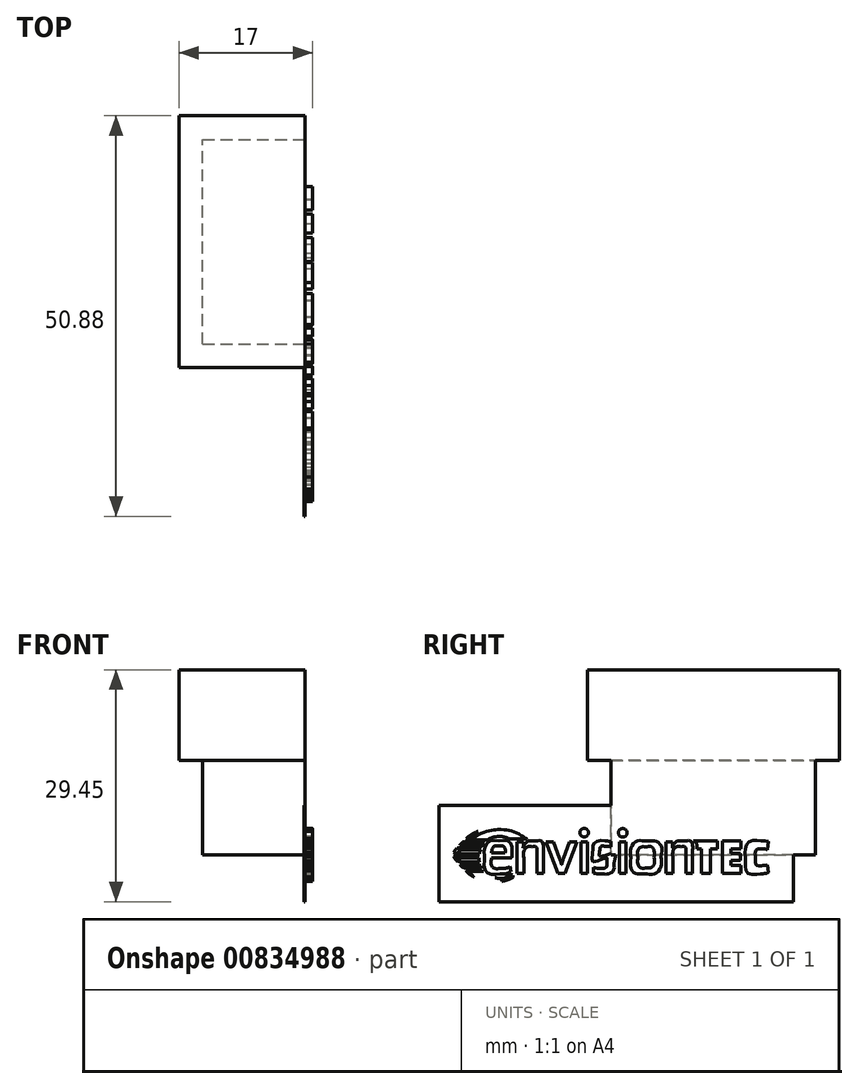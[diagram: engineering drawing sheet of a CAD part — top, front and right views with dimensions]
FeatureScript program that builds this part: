
annotation { "Feature Type Name" : "Feature", "Feature Type Description" : "" }
export const myFeature = defineFeature(function(context is Context, id is Id, definition is map)
    precondition{}
    {
        {
            var Q0;
            Q0=qCreatedBy(makeId("Top.planeOp"),FACE);
            var sketch = newSketch(context, id + "F0", { "sketchPlane" : qUnion([Q0])});
            skLineSegment(sketch, "E0.bottom", {"start": v(0, 0) * mm, "end": v(13, 0) * mm});
            skLineSegment(sketch, "E0.top", {"start": v(0, 26) * mm, "end": v(13, 26) * mm});
            skLineSegment(sketch, "E0.left", {"start": v(0, 0) * mm, "end": v(0, 26) * mm});
            skLineSegment(sketch, "E0.right", {"start": v(13, 0) * mm, "end": v(13, 26) * mm});
            skSolve(sketch);
        }
        {
            var Q0;
            Q0=makeQuery(id+"F0.imprint","IMPRINT",FACE,{"disambiguationData":[TD([[makeQuery(id+"F0.imprint","IMPRINT",EDGE,{"derivedFrom":sQuery(id+"F0.wireOp",EDGE,"E0.bottom")}),1.0]])]});
            extrude(context, id + "F1", {"entities" : qUnion([Q0]), "depth" : 22 * mm, "offsetDistance" : 25 * mm});
        }
        {
            var Q0;
            Q0=makeQuery(id+"F1.opExtrude","CAP_FACE",FACE,{"disambiguationData":[OSD([sQuery(id+"F0.wireOp",EDGE,"E0.bottom"),sQuery(id+"F0.wireOp",EDGE,"E0.top"),sQuery(id+"F0.wireOp",EDGE,"E0.left"),sQuery(id+"F0.wireOp",EDGE,"E0.right")])],"isStart":false});
            var sketch = newSketch(context, id + "F2", { "sketchPlane" : qUnion([Q0])});
            skLineSegment(sketch, "E1", {"start": v(13, 26) * mm, "end": v(13, 29) * mm});
            skLineSegment(sketch, "E2", {"start": v(13, 29) * mm, "end": v(-3, 29) * mm});
            skLineSegment(sketch, "E3", {"start": v(-3, 29) * mm, "end": v(-3, -3) * mm});
            skLineSegment(sketch, "E4", {"start": v(-3, -3) * mm, "end": v(13, -3) * mm});
            skLineSegment(sketch, "E5", {"start": v(13, -3) * mm, "end": v(13, 26) * mm});
            skSolve(sketch);
        }
        {
            var Q0;
            Q0=makeQuery(id+"F2.imprint","IMPRINT",FACE,{"disambiguationData":[TD([[makeQuery(id+"F2.imprint","IMPRINT",EDGE,{"derivedFrom":sQuery(id+"F2.wireOp",EDGE,"E1")}),1.0]])]});
            extrude(context, id + "F3", {"entities" : qUnion([Q0]), "oppositeDirection" : true, "depth" : 10 * mm, "offsetDistance" : 25 * mm});
        }
        {
            var Q0;
            Q0=makeQuery(id+"F3.opExtrude","CAP_FACE",FACE,{"disambiguationData":[OSD([sQuery(id+"F0.wireOp",EDGE,"E0.bottom"),sQuery(id+"F0.wireOp",EDGE,"E0.top"),sQuery(id+"F0.wireOp",EDGE,"E0.left"),sQuery(id+"F2.wireOp",EDGE,"E1"),sQuery(id+"F2.wireOp",EDGE,"E2"),sQuery(id+"F2.wireOp",EDGE,"E3"),sQuery(id+"F2.wireOp",EDGE,"E4"),sQuery(id+"F2.wireOp",EDGE,"E5")])],"isStart":true});
            var sketch = newSketch(context, id + "F4", { "sketchPlane" : qUnion([Q0])});
            skLineSegment(sketch, "E6.bottom", {"start": v(-3, 29) * mm, "end": v(13, 29) * mm});
            skLineSegment(sketch, "E6.top", {"start": v(-3, -3) * mm, "end": v(13, -3) * mm});
            skLineSegment(sketch, "E6.left", {"start": v(-3, 29) * mm, "end": v(-3, -3) * mm});
            skLineSegment(sketch, "E6.right", {"start": v(13, 29) * mm, "end": v(13, -3) * mm});
            skSolve(sketch);
        }
        {
            var Q0;
            Q0 = qSketchRegion(id + "F4", true);
            extrude(context, id + "F5", {"entities" : qUnion([Q0]), "operationType" : NewBodyOperationType.ADD, "depth" : 1.5 * mm, "offsetDistance" : 25 * mm});
        }
        {
            var Q0;
            Q0=makeQuery(id+"F1.opExtrude","SWEPT_FACE",FACE,{"disambiguationData":[OSD([sQuery(id+"F0.wireOp",EDGE,"E0.right")])]});
            var sketch = newSketch(context, id + "F6", { "sketchPlane" : qUnion([Q0])});
            skFitSpline(sketch, "E7", {"points": [v(-18.49, 1.44) * mm, v(-18.63, 1.49) * mm, v(-18.77, 1.54) * mm, v(-18.91, 1.58) * mm]});
            skFitSpline(sketch, "E8", {"points": [v(-18.91, 1.58) * mm, v(-19.01, 1.48) * mm, v(-19.1, 1.38) * mm, v(-19.19, 1.28) * mm]});
            skFitSpline(sketch, "E9", {"points": [v(-19.19, 1.28) * mm, v(-19.05, 1.23) * mm, v(-18.9, 1.18) * mm, v(-18.76, 1.14) * mm]});
            skFitSpline(sketch, "E10", {"points": [v(-18.76, 1.14) * mm, v(-18.63, 1.29) * mm, v(-18.6, 1.31) * mm, v(-18.49, 1.44) * mm]});
            skFitSpline(sketch, "E11", {"points": [v(-16.8, -0.4) * mm, v(-17.67, -0.4) * mm, v(-18.55, -0.4) * mm, v(-19.43, -0.4) * mm]});
            skFitSpline(sketch, "E12", {"points": [v(-19.43, -0.4) * mm, v(-19.36, -0.5) * mm, v(-19.1, -0.85) * mm, v(-19.06, -0.92) * mm]});
            skFitSpline(sketch, "E13", {"points": [v(-19.06, -0.92) * mm, v(-18.28, -0.92) * mm, v(-17.5, -0.92) * mm, v(-16.7, -0.92) * mm]});
            skFitSpline(sketch, "E14", {"points": [v(-16.7, -0.92) * mm, v(-16.76, -0.73) * mm, v(-16.79, -0.56) * mm, v(-16.8, -0.4) * mm]});
            skFitSpline(sketch, "E15", {"points": [v(-18.76, -1.4) * mm, v(-18.9, -1.35) * mm, v(-19.04, -1.3) * mm, v(-19.19, -1.25) * mm]});
            skFitSpline(sketch, "E16", {"points": [v(-19.19, -1.25) * mm, v(-19.1, -1.35) * mm, v(-19, -1.46) * mm, v(-18.91, -1.56) * mm]});
            skFitSpline(sketch, "E17", {"points": [v(-18.91, -1.56) * mm, v(-18.77, -1.6) * mm, v(-18.63, -1.65) * mm, v(-18.49, -1.7) * mm]});
            skFitSpline(sketch, "E18", {"points": [v(-18.49, -1.7) * mm, v(-18.58, -1.6) * mm, v(-18.67, -1.49) * mm, v(-18.76, -1.4) * mm]});
            skFitSpline(sketch, "E19", {"points": [v(-12.46, -2.63) * mm, v(-14.33, -3.43) * mm, v(-15.5, -2.93) * mm, v(-16.15, -2.17) * mm]});
            skFitSpline(sketch, "E20", {"points": [v(-16.15, -2.17) * mm, v(-16.72, -2.17) * mm, v(-17.28, -2.17) * mm, v(-17.84, -2.17) * mm]});
            skFitSpline(sketch, "E21", {"points": [v(-17.84, -2.17) * mm, v(-17.12, -2.75) * mm, v(-17.02, -2.77) * mm, v(-16.6, -2.98) * mm]});
            skFitSpline(sketch, "E22", {"points": [v(-15.52, -3.3) * mm, v(-15.33, -3.34) * mm, v(-15.12, -3.35) * mm, v(-14.91, -3.37) * mm]});
            skFitSpline(sketch, "E23", {"points": [v(-16.6, -2.98) * mm, v(-16.28, -3.13) * mm, v(-15.9, -3.22) * mm, v(-15.52, -3.3) * mm]});
            skFitSpline(sketch, "E24", {"points": [v(-14.46, -3.37) * mm, v(-13.84, -3.35) * mm, v(-13.16, -3.2) * mm, v(-12.43, -2.88) * mm]});
            skFitSpline(sketch, "E25", {"points": [v(-14.91, -3.37) * mm, v(-14.77, -3.37) * mm, v(-14.62, -3.38) * mm, v(-14.46, -3.37) * mm]});
            skFitSpline(sketch, "E26", {"points": [v(-12.43, -2.88) * mm, v(-12.44, -2.8) * mm, v(-12.45, -2.71) * mm, v(-12.46, -2.63) * mm]});
            skFitSpline(sketch, "E27", {"points": [v(-16.33, 1.13) * mm, v(-16.26, 1.23) * mm, v(-16.18, 1.33) * mm, v(-16.1, 1.42) * mm]});
            skFitSpline(sketch, "E28", {"points": [v(-16.1, 1.42) * mm, v(-16.86, 1.42) * mm, v(-17.63, 1.42) * mm, v(-18.39, 1.42) * mm]});
            skFitSpline(sketch, "E29", {"points": [v(-18.39, 1.42) * mm, v(-18.48, 1.32) * mm, v(-18.57, 1.23) * mm, v(-18.66, 1.13) * mm]});
            skFitSpline(sketch, "E30", {"points": [v(-18.66, 1.13) * mm, v(-17.88, 1.13) * mm, v(-17.1, 1.13) * mm, v(-16.33, 1.13) * mm]});
            skFitSpline(sketch, "E31", {"points": [v(-19.43, 0.14) * mm, v(-18.53, 0.14) * mm, v(-17.62, 0.13) * mm, v(-16.72, 0.13) * mm]});
            skFitSpline(sketch, "E32", {"points": [v(-16.72, 0.13) * mm, v(-16.68, 0.32) * mm, v(-16.61, 0.49) * mm, v(-16.54, 0.65) * mm]});
            skFitSpline(sketch, "E33", {"points": [v(-16.54, 0.65) * mm, v(-17.38, 0.65) * mm, v(-18.23, 0.65) * mm, v(-19.07, 0.65) * mm]});
            skFitSpline(sketch, "E34", {"points": [v(-19.07, 0.65) * mm, v(-19.2, 0.48) * mm, v(-19.3, 0.3) * mm, v(-19.43, 0.14) * mm]});
            skFitSpline(sketch, "E35", {"points": [v(-17, 0.88) * mm, v(-18.27, 0.88) * mm, v(-19.52, 0.88) * mm]});
            skFitSpline(sketch, "E36", {"points": [v(-19.52, 0.88) * mm, v(-19.28, 0.8) * mm, v(-19.03, 0.71) * mm]});
            skFitSpline(sketch, "E37", {"points": [v(-19.03, 0.71) * mm, v(-17.77, 0.71) * mm, v(-16.51, 0.71) * mm]});
            skFitSpline(sketch, "E38", {"points": [v(-16.51, 0.71) * mm, v(-16.76, 0.8) * mm, v(-17, 0.88) * mm]});
            skFitSpline(sketch, "E39", {"points": [v(-16.08, 1.5) * mm, v(-16.32, 1.57) * mm, v(-16.56, 1.65) * mm]});
            skFitSpline(sketch, "E40", {"points": [v(-16.56, 1.65) * mm, v(-17.7, 1.65) * mm, v(-18.84, 1.65) * mm]});
            skFitSpline(sketch, "E41", {"points": [v(-18.84, 1.65) * mm, v(-18.6, 1.57) * mm, v(-18.36, 1.5) * mm]});
            skFitSpline(sketch, "E42", {"points": [v(-18.36, 1.5) * mm, v(-17.22, 1.5) * mm, v(-16.08, 1.5) * mm]});
            skFitSpline(sketch, "E43", {"points": [v(-18.41, 2.07) * mm, v(-18.27, 2.03) * mm, v(-18.12, 1.98) * mm, v(-17.97, 1.93) * mm]});
            skFitSpline(sketch, "E44", {"points": [v(-17.97, 1.93) * mm, v(-16.13, 3.5) * mm, v(-12.93, 3.96) * mm, v(-10.72, 2) * mm]});
            skFitSpline(sketch, "E45", {"points": [v(-10.72, 2) * mm, v(-10.7, 2) * mm, v(-10.7, 2) * mm, v(-10.69, 2) * mm]});
            skFitSpline(sketch, "E46", {"points": [v(10.47, 1.74) * mm, v(10.78, 1.6) * mm, v(10.94, 1.14) * mm, v(10.95, 0.77) * mm]});
            skFitSpline(sketch, "E47", {"points": [v(10.95, 0.77) * mm, v(11.14, 0.77) * mm, v(11.32, 0.77) * mm, v(11.5, 0.77) * mm]});
            skFitSpline(sketch, "E48", {"points": [v(11.5, 0.77) * mm, v(11.5, -0.26) * mm, v(11.5, -1.3) * mm, v(11.5, -2.34) * mm]});
            skFitSpline(sketch, "E49", {"points": [v(11.5, -2.34) * mm, v(11.89, -2.34) * mm, v(12.26, -2.34) * mm, v(12.64, -2.34) * mm]});
            skFitSpline(sketch, "E50", {"points": [v(12.64, -2.34) * mm, v(12.64, -1.3) * mm, v(12.64, -0.26) * mm, v(12.64, 0.77) * mm]});
            skFitSpline(sketch, "E51", {"points": [v(12.64, 0.77) * mm, v(12.93, 0.77) * mm, v(13.23, 0.77) * mm, v(13.52, 0.77) * mm]});
            skFitSpline(sketch, "E52", {"points": [v(13.52, 0.77) * mm, v(13.52, 1.1) * mm, v(13.52, 1.42) * mm, v(13.52, 1.74) * mm]});
            skFitSpline(sketch, "E53", {"points": [v(13.52, 1.74) * mm, v(12.5, 1.74) * mm, v(11.49, 1.74) * mm, v(10.47, 1.74) * mm]});
            skFitSpline(sketch, "E54", {"points": [v(10.37, -2.33) * mm, v(10.37, -1.4) * mm, v(10.37, -0.46) * mm, v(10.37, 0.47) * mm]});
            skFitSpline(sketch, "E55", {"points": [v(10.37, 0.47) * mm, v(10.37, 1.18) * mm, v(10.09, 1.76) * mm, v(9.18, 1.76) * mm, v(8.5, 1.76) * mm, v(8.02, 1.4) * mm, v(7.78, 0.88) * mm]});
            skFitSpline(sketch, "E56", {"points": [v(7.78, 0.88) * mm, v(7.78, 0.89) * mm, v(7.78, 0.9) * mm, v(7.77, 0.9) * mm]});
            skFitSpline(sketch, "E57", {"points": [v(7.78, 0.88) * mm, v(7.78, 0.89) * mm, v(7.78, 0.9) * mm, v(7.77, 0.9) * mm]});
            skFitSpline(sketch, "E58", {"points": [v(7.77, 0.9) * mm, v(7.81, 1.12) * mm, v(7.83, 1.46) * mm, v(7.83, 1.67) * mm]});
            skFitSpline(sketch, "E59", {"points": [v(7.83, 1.67) * mm, v(7.56, 1.67) * mm, v(7.28, 1.67) * mm, v(7, 1.67) * mm]});
            skFitSpline(sketch, "E60", {"points": [v(7, 1.67) * mm, v(7, 0.34) * mm, v(7, -1) * mm, v(7, -2.33) * mm]});
            skFitSpline(sketch, "E61", {"points": [v(7, -2.33) * mm, v(7.3, -2.33) * mm, v(7.58, -2.33) * mm, v(7.87, -2.33) * mm]});
            skFitSpline(sketch, "E62", {"points": [v(7.87, -2.33) * mm, v(7.87, -1.68) * mm, v(7.87, -1.04) * mm, v(7.87, -0.4) * mm]});
            skFitSpline(sketch, "E63", {"points": [v(7.87, -0.4) * mm, v(7.87, 0.4) * mm, v(8.31, 1.04) * mm, v(8.92, 1.04) * mm, v(9.38, 1.04) * mm, v(9.51, 0.75) * mm, v(9.51, 0.25) * mm]});
            skFitSpline(sketch, "E64", {"points": [v(9.51, 0.25) * mm, v(9.51, -0.61) * mm, v(9.51, -1.47) * mm, v(9.51, -2.33) * mm]});
            skFitSpline(sketch, "E65", {"points": [v(9.51, -2.33) * mm, v(9.8, -2.33) * mm, v(10.08, -2.33) * mm, v(10.37, -2.33) * mm]});
            skFitSpline(sketch, "E66", {"points": [v(2.54, -0.38) * mm, v(2.54, -1.79) * mm, v(3.26, -2.4) * mm, v(4.37, -2.4) * mm, v(5.56, -2.4) * mm, v(6.36, -1.48) * mm, v(6.36, -0.25) * mm]});
            skFitSpline(sketch, "E67", {"points": [v(6.36, -0.25) * mm, v(6.36, 1.16) * mm, v(5.6, 1.76) * mm, v(4.53, 1.76) * mm, v(3.32, 1.76) * mm, v(2.54, 0.83) * mm, v(2.54, -0.38) * mm]});
            skFitSpline(sketch, "E68", {"points": [v(3.43, -0.3) * mm, v(3.43, 0.63) * mm, v(3.94, 1.03) * mm, v(4.46, 1.03) * mm, v(5.14, 1.03) * mm, v(5.48, 0.55) * mm, v(5.48, -0.3) * mm]});
            skFitSpline(sketch, "E69", {"points": [v(5.48, -0.3) * mm, v(5.48, -1.23) * mm, v(5, -1.67) * mm, v(4.45, -1.67) * mm, v(3.78, -1.67) * mm, v(3.43, -1.2) * mm, v(3.43, -0.3) * mm]});
            skFitSpline(sketch, "E70", {"points": [v(1.93, 1.67) * mm, v(1.5, 1.67) * mm, v(1.07, 1.67) * mm]});
            skFitSpline(sketch, "E71", {"points": [v(1.07, 1.67) * mm, v(1.07, -0.33) * mm, v(1.07, -2.33) * mm]});
            skFitSpline(sketch, "E72", {"points": [v(1.07, -2.33) * mm, v(1.5, -2.33) * mm, v(1.93, -2.33) * mm]});
            skFitSpline(sketch, "E73", {"points": [v(1.93, -2.33) * mm, v(1.93, -0.33) * mm, v(1.93, 1.67) * mm]});
            skFitSpline(sketch, "E74", {"points": [v(0.36, -1.11) * mm, v(0.36, 0.22) * mm, v(-1.4, -0.18) * mm, v(-1.4, 0.6) * mm, v(-1.4, 0.9) * mm, v(-1.18, 1.1) * mm, v(-0.7, 1.1) * mm, v(-0.44, 1.1) * mm, v(-0.16, 1.05) * mm, v(0.08, 0.98) * mm]});
            skFitSpline(sketch, "E75", {"points": [v(0.08, 0.98) * mm, v(0.09, 1.22) * mm, v(0.1, 1.45) * mm, v(0.1, 1.68) * mm]});
            skFitSpline(sketch, "E76", {"points": [v(0.1, 1.68) * mm, v(-0.14, 1.72) * mm, v(-0.41, 1.76) * mm, v(-0.64, 1.76) * mm, v(-1.73, 1.76) * mm, v(-2.3, 1.2) * mm, v(-2.3, 0.51) * mm, v(-2.3, -0.87) * mm, v(-0.54, -0.39) * mm, v(-0.54, -1.2) * mm, v(-0.54, -1.52) * mm, v(-0.86, -1.72) * mm, v(-1.33, -1.72) * mm, v(-1.63, -1.72) * mm, v(-1.95, -1.67) * mm, v(-2.2, -1.6) * mm]});
            skFitSpline(sketch, "E77", {"points": [v(-2.2, -1.6) * mm, v(-2.2, -1.84) * mm, v(-2.21, -2.08) * mm, v(-2.22, -2.33) * mm]});
            skFitSpline(sketch, "E78", {"points": [v(-2.22, -2.33) * mm, v(-1.97, -2.38) * mm, v(-1.67, -2.4) * mm, v(-1.38, -2.4) * mm, v(-0.3, -2.4) * mm, v(0.36, -1.86) * mm, v(0.36, -1.11) * mm]});
            skFitSpline(sketch, "E79", {"points": [v(-2.98, 1.67) * mm, v(-3.41, 1.67) * mm, v(-3.84, 1.67) * mm]});
            skFitSpline(sketch, "E80", {"points": [v(-3.84, 1.67) * mm, v(-3.84, -0.33) * mm, v(-3.84, -2.33) * mm]});
            skFitSpline(sketch, "E81", {"points": [v(-3.84, -2.33) * mm, v(-3.41, -2.33) * mm, v(-2.98, -2.33) * mm]});
            skFitSpline(sketch, "E82", {"points": [v(-2.98, -2.33) * mm, v(-2.98, -0.33) * mm, v(-2.98, 1.67) * mm]});
            skFitSpline(sketch, "E83", {"points": [v(-4.35, 1.67) * mm, v(-4.65, 1.67) * mm, v(-4.96, 1.67) * mm, v(-5.27, 1.67) * mm]});
            skFitSpline(sketch, "E84", {"points": [v(-5.27, 1.67) * mm, v(-5.53, 0.96) * mm, v(-5.78, 0.24) * mm, v(-6.04, -0.48) * mm]});
            skFitSpline(sketch, "E85", {"points": [v(-6.04, -0.48) * mm, v(-6.13, -0.73) * mm, v(-6.2, -1.02) * mm, v(-6.27, -1.27) * mm]});
            skFitSpline(sketch, "E86", {"points": [v(-6.27, -1.27) * mm, v(-6.27, -1.27) * mm, v(-6.28, -1.27) * mm, v(-6.28, -1.27) * mm]});
            skFitSpline(sketch, "E87", {"points": [v(-6.27, -1.27) * mm, v(-6.27, -1.27) * mm, v(-6.28, -1.27) * mm, v(-6.28, -1.27) * mm]});
            skFitSpline(sketch, "E88", {"points": [v(-6.28, -1.27) * mm, v(-6.35, -1) * mm, v(-6.44, -0.72) * mm, v(-6.54, -0.44) * mm]});
            skFitSpline(sketch, "E89", {"points": [v(-6.54, -0.44) * mm, v(-6.79, 0.26) * mm, v(-7.04, 0.97) * mm, v(-7.29, 1.67) * mm]});
            skFitSpline(sketch, "E90", {"points": [v(-7.29, 1.67) * mm, v(-7.6, 1.67) * mm, v(-7.92, 1.67) * mm, v(-8.24, 1.67) * mm]});
            skFitSpline(sketch, "E91", {"points": [v(-8.24, 1.67) * mm, v(-7.74, 0.34) * mm, v(-7.24, -1) * mm, v(-6.74, -2.33) * mm]});
            skFitSpline(sketch, "E92", {"points": [v(-6.74, -2.33) * mm, v(-6.44, -2.33) * mm, v(-6.15, -2.33) * mm, v(-5.86, -2.33) * mm]});
            skFitSpline(sketch, "E93", {"points": [v(-5.86, -2.33) * mm, v(-5.35, -1) * mm, v(-4.85, 0.34) * mm, v(-4.35, 1.67) * mm]});
            skFitSpline(sketch, "E94", {"points": [v(-8.57, -2.33) * mm, v(-8.57, -1.4) * mm, v(-8.57, -0.46) * mm, v(-8.57, 0.47) * mm]});
            skFitSpline(sketch, "E95", {"points": [v(-8.57, 0.47) * mm, v(-8.57, 1.18) * mm, v(-8.85, 1.76) * mm, v(-9.76, 1.76) * mm, v(-10.44, 1.76) * mm, v(-10.92, 1.4) * mm, v(-11.16, 0.88) * mm]});
            skFitSpline(sketch, "E96", {"points": [v(-11.16, 0.88) * mm, v(-11.16, 0.89) * mm, v(-11.16, 0.9) * mm, v(-11.16, 0.9) * mm]});
            skFitSpline(sketch, "E97", {"points": [v(-11.16, 0.88) * mm, v(-11.16, 0.89) * mm, v(-11.16, 0.9) * mm, v(-11.16, 0.9) * mm]});
            skFitSpline(sketch, "E98", {"points": [v(-11.16, 0.9) * mm, v(-11.12, 1.12) * mm, v(-11.1, 1.46) * mm, v(-11.1, 1.67) * mm]});
            skFitSpline(sketch, "E99", {"points": [v(-11.1, 1.67) * mm, v(-11.38, 1.67) * mm, v(-11.65, 1.67) * mm, v(-11.93, 1.67) * mm]});
            skFitSpline(sketch, "E100", {"points": [v(-11.93, 1.67) * mm, v(-11.93, 0.34) * mm, v(-11.93, -1) * mm, v(-11.93, -2.33) * mm]});
            skFitSpline(sketch, "E101", {"points": [v(-11.93, -2.33) * mm, v(-11.64, -2.33) * mm, v(-11.35, -2.33) * mm, v(-11.07, -2.33) * mm]});
            skFitSpline(sketch, "E102", {"points": [v(-11.07, -2.33) * mm, v(-11.07, -1.68) * mm, v(-11.07, -1.04) * mm, v(-11.07, -0.4) * mm]});
            skFitSpline(sketch, "E103", {"points": [v(-11.07, -0.4) * mm, v(-11.07, 0.4) * mm, v(-10.62, 1.04) * mm, v(-10.02, 1.04) * mm, v(-9.56, 1.04) * mm, v(-9.42, 0.75) * mm, v(-9.42, 0.25) * mm]});
            skFitSpline(sketch, "E104", {"points": [v(-9.42, 0.25) * mm, v(-9.42, -0.61) * mm, v(-9.42, -1.47) * mm, v(-9.42, -2.33) * mm]});
            skFitSpline(sketch, "E105", {"points": [v(-9.42, -2.33) * mm, v(-9.14, -2.33) * mm, v(-8.85, -2.33) * mm, v(-8.57, -2.33) * mm]});
            skFitSpline(sketch, "E106", {"points": [v(20, -2.26) * mm, v(19.96, -1.92) * mm, v(19.91, -1.59) * mm, v(19.87, -1.25) * mm]});
            skFitSpline(sketch, "E107", {"points": [v(19.87, -1.25) * mm, v(19.7, -1.33) * mm, v(19.42, -1.37) * mm, v(19.25, -1.37) * mm, v(18.61, -1.37) * mm, v(18.34, -0.99) * mm, v(18.34, -0.28) * mm, v(18.34, 0.38) * mm, v(18.67, 0.75) * mm, v(19.2, 0.75) * mm, v(19.44, 0.75) * mm, v(19.67, 0.71) * mm, v(19.87, 0.66) * mm]});
            skFitSpline(sketch, "E108", {"points": [v(19.87, 0.66) * mm, v(19.9, 1) * mm, v(19.95, 1.34) * mm, v(20, 1.68) * mm]});
            skFitSpline(sketch, "E109", {"points": [v(20, 1.68) * mm, v(19.76, 1.74) * mm, v(19.47, 1.77) * mm, v(19.2, 1.77) * mm, v(17.87, 1.77) * mm, v(17.1, 0.9) * mm, v(17.1, -0.47) * mm, v(17.1, -1.3) * mm, v(17.43, -2.4) * mm, v(19.04, -2.4) * mm, v(19.36, -2.4) * mm, v(19.72, -2.35) * mm, v(20, -2.26) * mm]});
            skFitSpline(sketch, "E110", {"points": [v(16.52, -2.34) * mm, v(16.52, -1.86) * mm, v(16.52, -1.37) * mm]});
            skFitSpline(sketch, "E111", {"points": [v(16.52, -1.37) * mm, v(15.9, -1.37) * mm, v(15.26, -1.37) * mm]});
            skFitSpline(sketch, "E112", {"points": [v(15.26, -1.37) * mm, v(15.26, -1.04) * mm, v(15.26, -0.7) * mm]});
            skFitSpline(sketch, "E113", {"points": [v(15.26, -0.7) * mm, v(15.86, -0.7) * mm, v(16.46, -0.7) * mm]});
            skFitSpline(sketch, "E114", {"points": [v(16.46, -0.7) * mm, v(16.46, -0.25) * mm, v(16.46, 0.21) * mm]});
            skFitSpline(sketch, "E115", {"points": [v(16.46, 0.21) * mm, v(15.86, 0.21) * mm, v(15.26, 0.21) * mm]});
            skFitSpline(sketch, "E116", {"points": [v(15.26, 0.21) * mm, v(15.26, 0.5) * mm, v(15.26, 0.79) * mm]});
            skFitSpline(sketch, "E117", {"points": [v(15.26, 0.79) * mm, v(15.9, 0.79) * mm, v(16.52, 0.79) * mm]});
            skFitSpline(sketch, "E118", {"points": [v(16.52, 0.79) * mm, v(16.52, 1.27) * mm, v(16.52, 1.74) * mm]});
            skFitSpline(sketch, "E119", {"points": [v(16.52, 1.74) * mm, v(15.33, 1.74) * mm, v(14.13, 1.74) * mm]});
            skFitSpline(sketch, "E120", {"points": [v(14.13, 1.74) * mm, v(14.13, -0.3) * mm, v(14.13, -2.34) * mm]});
            skFitSpline(sketch, "E121", {"points": [v(14.13, -2.34) * mm, v(15.33, -2.34) * mm, v(16.52, -2.34) * mm]});
            skFitSpline(sketch, "E122", {"points": [v(-12.59, 0.02) * mm, v(-12.59, 0.98) * mm, v(-13.08, 1.76) * mm, v(-14.23, 1.76) * mm, v(-15.4, 1.76) * mm, v(-16.06, 0.86) * mm, v(-16.06, -0.36) * mm, v(-16.06, -1.77) * mm, v(-15.38, -2.42) * mm, v(-14.12, -2.42) * mm, v(-13.63, -2.42) * mm, v(-13.14, -2.33) * mm, v(-12.73, -2.16) * mm]});
            skFitSpline(sketch, "E123", {"points": [v(-12.73, -2.16) * mm, v(-12.76, -1.93) * mm, v(-12.79, -1.7) * mm, v(-12.81, -1.47) * mm]});
            skFitSpline(sketch, "E124", {"points": [v(-12.81, -1.47) * mm, v(-13.14, -1.63) * mm, v(-13.57, -1.73) * mm, v(-13.99, -1.73) * mm, v(-14.79, -1.73) * mm, v(-15.2, -1.31) * mm, v(-15.17, -0.38) * mm]});
            skFitSpline(sketch, "E125", {"points": [v(-12.81, -1.47) * mm, v(-13.14, -1.63) * mm, v(-13.57, -1.73) * mm, v(-13.99, -1.73) * mm, v(-14.79, -1.73) * mm, v(-15.2, -1.31) * mm, v(-15.17, -0.38) * mm]});
            skFitSpline(sketch, "E126", {"points": [v(-15.17, -0.38) * mm, v(-14.32, -0.38) * mm, v(-13.46, -0.38) * mm, v(-12.6, -0.38) * mm]});
            skFitSpline(sketch, "E127", {"points": [v(-12.6, -0.38) * mm, v(-12.6, -0.23) * mm, v(-12.59, -0.09) * mm, v(-12.59, 0.02) * mm]});
            skFitSpline(sketch, "E128", {"points": [v(-13.45, 0.23) * mm, v(-14.02, 0.23) * mm, v(-14.59, 0.23) * mm, v(-15.16, 0.23) * mm]});
            skFitSpline(sketch, "E129", {"points": [v(-15.16, 0.23) * mm, v(-15.09, 0.77) * mm, v(-14.75, 1.12) * mm, v(-14.26, 1.12) * mm, v(-13.75, 1.12) * mm, v(-13.43, 0.78) * mm, v(-13.45, 0.23) * mm]});
            skFitSpline(sketch, "E130", {"points": [v(-18.4, -1.95) * mm, v(-18.16, -2.03) * mm, v(-17.91, -2.1) * mm]});
            skFitSpline(sketch, "E131", {"points": [v(-17.91, -2.1) * mm, v(-17.05, -2.1) * mm, v(-16.2, -2.1) * mm]});
            skFitSpline(sketch, "E132", {"points": [v(-16.2, -2.1) * mm, v(-16.44, -2.03) * mm, v(-16.68, -1.95) * mm]});
            skFitSpline(sketch, "E133", {"points": [v(-16.68, -1.95) * mm, v(-17.54, -1.95) * mm, v(-18.4, -1.95) * mm]});
            skFitSpline(sketch, "E134", {"points": [v(-17.85, 1.9) * mm, v(-17.16, 1.9) * mm, v(-16.48, 1.9) * mm, v(-15.8, 1.9) * mm, v(-15.76, 1.9) * mm, v(-15.72, 1.9) * mm, v(-15.68, 1.9) * mm]});
            skFitSpline(sketch, "E135", {"points": [v(-14.87, 2.27) * mm, v(-14.02, 2.44) * mm, v(-13.15, 2.24) * mm, v(-12.84, 2) * mm]});
            skFitSpline(sketch, "E136", {"points": [v(-12.84, 2) * mm, v(-11.25, 2) * mm, v(-11.25, 2) * mm]});
            skFitSpline(sketch, "E137", {"points": [v(-11.25, 2) * mm, v(-11.25, 2) * mm, v(-10.8, 2) * mm]});
            skFitSpline(sketch, "E138", {"points": [v(-14.33, 3.21) * mm, v(-14.33, 3.21) * mm, v(-14.33, 3.21) * mm, v(-14.33, 3.21) * mm]});
            skFitSpline(sketch, "E139", {"points": [v(-14.33, 3.21) * mm, v(-14.33, 3.21) * mm, v(-14.33, 3.21) * mm, v(-14.33, 3.21) * mm]});
            skFitSpline(sketch, "E140", {"points": [v(-20, -0.18) * mm, v(-19.73, -0.25) * mm, v(-19.46, -0.33) * mm]});
            skFitSpline(sketch, "E141", {"points": [v(-19.46, -0.33) * mm, v(-18.13, -0.33) * mm, v(-16.8, -0.33) * mm]});
            skFitSpline(sketch, "E142", {"points": [v(-16.8, -0.33) * mm, v(-17.03, -0.25) * mm, v(-17.26, -0.18) * mm]});
            skFitSpline(sketch, "E143", {"points": [v(-17.26, -0.18) * mm, v(-18.63, -0.18) * mm, v(-20, -0.18) * mm]});
            skFitSpline(sketch, "E144", {"points": [v(-14.7, -2.92) * mm, v(-14.26, -3) * mm, v(-13.4, -3) * mm, v(-12.49, -2.54) * mm]});
            skFitSpline(sketch, "E145", {"points": [v(-12.49, -2.54) * mm, v(-12.57, -2.52) * mm, v(-12.65, -2.5) * mm, v(-12.73, -2.47) * mm]});
            skFitSpline(sketch, "E146", {"points": [v(-12.73, -2.47) * mm, v(-13.67, -2.98) * mm, v(-14.7, -2.92) * mm]});
            skFitSpline(sketch, "E147", {"points": [v(-20, -0.24) * mm, v(-19.86, -0.37) * mm, v(-19.73, -0.6) * mm, v(-19.6, -0.77) * mm]});
            skFitSpline(sketch, "E148", {"points": [v(-19.6, -0.77) * mm, v(-19.45, -0.82) * mm, v(-19.3, -0.86) * mm, v(-19.16, -0.91) * mm]});
            skFitSpline(sketch, "E149", {"points": [v(-19.16, -0.91) * mm, v(-19.31, -0.7) * mm, v(-19.5, -0.42) * mm, v(-19.53, -0.4) * mm]});
            skFitSpline(sketch, "E150", {"points": [v(-19.53, -0.4) * mm, v(-19.69, -0.34) * mm, v(-19.84, -0.29) * mm, v(-20, -0.24) * mm]});
            skFitSpline(sketch, "E151", {"points": [v(-19.53, 0.14) * mm, v(-19.4, 0.34) * mm, v(-19.3, 0.48) * mm, v(-19.17, 0.67) * mm]});
            skFitSpline(sketch, "E152", {"points": [v(-19.17, 0.67) * mm, v(-19.31, 0.72) * mm, v(-19.45, 0.77) * mm, v(-19.6, 0.82) * mm]});
            skFitSpline(sketch, "E153", {"points": [v(-19.6, 0.82) * mm, v(-19.73, 0.65) * mm, v(-19.86, 0.48) * mm, v(-20, 0.3) * mm]});
            skFitSpline(sketch, "E154", {"points": [v(-20, 0.3) * mm, v(-19.84, 0.25) * mm, v(-19.69, 0.2) * mm, v(-19.53, 0.14) * mm]});
            skFitSpline(sketch, "E155", {"points": [v(-17.95, -2.17) * mm, v(-18.1, -2.12) * mm, v(-18.26, -2.07) * mm, v(-18.41, -2.02) * mm]});
            skFitSpline(sketch, "E156", {"points": [v(-18.41, -2.02) * mm, v(-17.96, -2.48) * mm, v(-17.23, -2.89) * mm, v(-16.58, -3.12) * mm]});
            skFitSpline(sketch, "E157", {"points": [v(-16.57, -1.4) * mm, v(-17.27, -1.4) * mm, v(-17.96, -1.4) * mm, v(-18.66, -1.4) * mm]});
            skFitSpline(sketch, "E158", {"points": [v(-18.66, -1.4) * mm, v(-18.57, -1.5) * mm, v(-18.48, -1.6) * mm, v(-18.39, -1.7) * mm]});
            skFitSpline(sketch, "E159", {"points": [v(-18.39, -1.7) * mm, v(-17.73, -1.7) * mm, v(-17.07, -1.7) * mm, v(-16.42, -1.7) * mm]});
            skFitSpline(sketch, "E160", {"points": [v(-16.42, -1.7) * mm, v(-16.48, -1.6) * mm, v(-16.53, -1.5) * mm, v(-16.57, -1.4) * mm]});
            skFitSpline(sketch, "E161", {"points": [v(-19.18, -1.17) * mm, v(-18.94, -1.25) * mm, v(-18.7, -1.33) * mm]});
            skFitSpline(sketch, "E162", {"points": [v(-18.7, -1.33) * mm, v(-17.65, -1.33) * mm, v(-16.6, -1.33) * mm]});
            skFitSpline(sketch, "E163", {"points": [v(-16.6, -1.33) * mm, v(-16.84, -1.25) * mm, v(-17.08, -1.17) * mm]});
            skFitSpline(sketch, "E164", {"points": [v(-17.08, -1.17) * mm, v(-18.13, -1.17) * mm, v(-19.18, -1.17) * mm]});
            skFitSpline(sketch, "E165.trimOffspring", {"points": [v(-15.14, -3.4) * mm, v(-16.68, -3.36) * mm, v(-17.95, -2.17) * mm]});
            skLineSegment(sketch, "E166", {"start": v(-16.58, -3.12) * mm, "end": v(-16.11, -3.25) * mm});
            skFitSpline(sketch, "E167", {"points": [v(-18.41, 2.07) * mm, v(-16.73, 3.05) * mm, v(-14.17, 3.4) * mm, v(-13.48, 3.33) * mm, v(-12.87, 3.2) * mm, v(-12.37, 3.04) * mm, v(-11.96, 2.87) * mm, v(-11.5, 2.63) * mm, v(-11.27, 2.49) * mm, v(-11, 2.29) * mm, v(-10.74, 2.06) * mm, v(-10.69, 2) * mm], "startDerivative": vector(7.32, 6.17) * mm, "endDerivative": vector(1.19, -1.2) * mm});
            skFitSpline(sketch, "E168", {"points": [v(-17.85, 1.9) * mm, v(-17.54, 2.13) * mm, v(-17.17, 2.38) * mm, v(-16.86, 2.55) * mm, v(-16.5, 2.72) * mm, v(-16, 2.9) * mm, v(-15.62, 3.02) * mm, v(-15.19, 3.12) * mm, v(-14.84, 3.18) * mm, v(-14.65, 3.2) * mm, v(-14.26, 3.22) * mm, v(-13.64, 3.2) * mm, v(-13.28, 3.15) * mm, v(-12.9, 3.08) * mm, v(-12.45, 2.96) * mm, v(-12.06, 2.81) * mm, v(-11.6, 2.59) * mm, v(-11.08, 2.24) * mm, v(-10.8, 2) * mm], "startDerivative": vector(5.49, 4.37) * mm, "endDerivative": vector(4.8, -4.37) * mm});
            skFitSpline(sketch, "E169", {"points": [v(-15.68, 1.9) * mm, v(-15.51, 2) * mm, v(-15.32, 2.1) * mm, v(-15.06, 2.21) * mm, v(-14.93, 2.25) * mm, v(-14.79, 2.28) * mm, v(-14.49, 2.32) * mm, v(-14.21, 2.33) * mm, v(-13.97, 2.32) * mm, v(-13.73, 2.3) * mm, v(-13.5, 2.26) * mm, v(-13.32, 2.21) * mm, v(-13.15, 2.16) * mm, v(-13, 2.1) * mm, v(-12.9, 2.04) * mm, v(-12.84, 2) * mm], "startDerivative": vector(2.46, 1.6) * mm, "endDerivative": vector(1.36, -0.96) * mm});
            skCircle(sketch, "E170", {"center": v(-3.4, 2.81) * mm, "radius": 0.54 * mm});
            skPoint(sketch, "E170.first.point", {"position": v(-3.75, 3.24) * mm});
            skPoint(sketch, "E170.second.point", {"position": v(-3.63, 2.32) * mm});
            skPoint(sketch, "E170.third.point", {"position": v(-2.98, 3.15) * mm});
            skCircle(sketch, "E171", {"center": v(1.5, 2.8) * mm, "radius": 0.55 * mm});
            skPoint(sketch, "E171.third.point", {"position": v(1.55, 3.35) * mm});
            skSolve(sketch);
        }
        {
            var Q0;
            {var subQ4=sQuery(id+"F6.wireOp",EDGE,"E167");Q0=makeQuery(id+"F6.imprint","IMPRINT",FACE,{"disambiguationData":[TD([[makeQuery(id+"F6.imprint","IMPRINT",EDGE,{"derivedFrom":subQ4}),-1.0]])]});}
            var Q1;
            {var subQ5=sQuery(id+"F6.wireOp",EDGE,"8eT48PlR-omNr-KQEF-wRAB-eHz9Z6P4Qwk8");Q1=makeQuery(id+"F6.imprint","IMPRINT",FACE,{"disambiguationData":[TD([[makeQuery(id+"F6.imprint","IMPRINT",EDGE,{"derivedFrom":subQ5}),-1.0]])]});}
            var Q2;
            Q2=makeQuery(id+"F6.imprint","IMPRINT",FACE,{"disambiguationData":[TD([[makeQuery(id+"F6.imprint","IMPRINT",EDGE,{"derivedFrom":sQuery(id+"F6.wireOp",EDGE,"E39")}),1.0]])]});
            var Q3;
            Q3=makeQuery(id+"F6.imprint","IMPRINT",FACE,{"disambiguationData":[TD([[makeQuery(id+"F6.imprint","IMPRINT",EDGE,{"derivedFrom":sQuery(id+"F6.wireOp",EDGE,"E27")}),1.0]])]});
            var Q4;
            Q4=makeQuery(id+"F6.imprint","IMPRINT",FACE,{"disambiguationData":[TD([[makeQuery(id+"F6.imprint","IMPRINT",EDGE,{"derivedFrom":sQuery(id+"F6.wireOp",EDGE,"E7")}),1.0]])]});
            var Q5;
            Q5=makeQuery(id+"F6.imprint","IMPRINT",FACE,{"disambiguationData":[TD([[makeQuery(id+"F6.imprint","IMPRINT",EDGE,{"derivedFrom":sQuery(id+"F6.wireOp",EDGE,"E35")}),1.0]])]});
            var Q6;
            Q6=makeQuery(id+"F6.imprint","IMPRINT",FACE,{"disambiguationData":[TD([[makeQuery(id+"F6.imprint","IMPRINT",EDGE,{"derivedFrom":sQuery(id+"F6.wireOp",EDGE,"E151")}),1.0]])]});
            var Q7;
            Q7=makeQuery(id+"F6.imprint","IMPRINT",FACE,{"disambiguationData":[TD([[makeQuery(id+"F6.imprint","IMPRINT",EDGE,{"derivedFrom":sQuery(id+"F6.wireOp",EDGE,"E31")}),1.0]])]});
            var Q8;
            Q8=makeQuery(id+"F6.imprint","IMPRINT",FACE,{"disambiguationData":[TD([[makeQuery(id+"F6.imprint","IMPRINT",EDGE,{"derivedFrom":sQuery(id+"F6.wireOp",EDGE,"E11")}),1.0]])]});
            var Q9;
            Q9=makeQuery(id+"F6.imprint","IMPRINT",FACE,{"disambiguationData":[TD([[makeQuery(id+"F6.imprint","IMPRINT",EDGE,{"derivedFrom":sQuery(id+"F6.wireOp",EDGE,"E140")}),1.0]])]});
            var Q10;
            Q10=makeQuery(id+"F6.imprint","IMPRINT",FACE,{"disambiguationData":[TD([[makeQuery(id+"F6.imprint","IMPRINT",EDGE,{"derivedFrom":sQuery(id+"F6.wireOp",EDGE,"E147")}),1.0]])]});
            var Q11;
            Q11=makeQuery(id+"F6.imprint","IMPRINT",FACE,{"disambiguationData":[TD([[makeQuery(id+"F6.imprint","IMPRINT",EDGE,{"derivedFrom":sQuery(id+"F6.wireOp",EDGE,"E122")}),1.0]])]});
            var Q12;
            Q12=makeQuery(id+"F6.imprint","IMPRINT",FACE,{"disambiguationData":[TD([[makeQuery(id+"F6.imprint","IMPRINT",EDGE,{"derivedFrom":sQuery(id+"F6.wireOp",EDGE,"E161")}),1.0]])]});
            var Q13;
            Q13=makeQuery(id+"F6.imprint","IMPRINT",FACE,{"disambiguationData":[TD([[makeQuery(id+"F6.imprint","IMPRINT",EDGE,{"derivedFrom":sQuery(id+"F6.wireOp",EDGE,"E157")}),1.0]])]});
            var Q14;
            Q14=makeQuery(id+"F6.imprint","IMPRINT",FACE,{"disambiguationData":[TD([[makeQuery(id+"F6.imprint","IMPRINT",EDGE,{"derivedFrom":sQuery(id+"F6.wireOp",EDGE,"E15")}),1.0]])]});
            var Q15;
            Q15=makeQuery(id+"F6.imprint","IMPRINT",FACE,{"disambiguationData":[TD([[makeQuery(id+"F6.imprint","IMPRINT",EDGE,{"derivedFrom":sQuery(id+"F6.wireOp",EDGE,"E130")}),1.0]])]});
            var Q16;
            Q16=makeQuery(id+"F6.imprint","IMPRINT",FACE,{"disambiguationData":[TD([[makeQuery(id+"F6.imprint","IMPRINT",EDGE,{"derivedFrom":sQuery(id+"F6.wireOp",EDGE,"E19")}),1.0]])]});
            var Q17;
            Q17=makeQuery(id+"F6.imprint","IMPRINT",FACE,{"disambiguationData":[TD([[makeQuery(id+"F6.imprint","IMPRINT",EDGE,{"derivedFrom":sQuery(id+"F6.wireOp",EDGE,"E155")}),1.0]])]});
            var Q18;
            Q18=makeQuery(id+"F6.imprint","IMPRINT",FACE,{"disambiguationData":[TD([[makeQuery(id+"F6.imprint","IMPRINT",EDGE,{"derivedFrom":sQuery(id+"F6.wireOp",EDGE,"E144")}),1.0]])]});
            var Q19;
            Q19=makeQuery(id+"F6.imprint","IMPRINT",FACE,{"disambiguationData":[TD([[makeQuery(id+"F6.imprint","IMPRINT",EDGE,{"derivedFrom":sQuery(id+"F6.wireOp",EDGE,"E94")}),1.0]])]});
            var Q20;
            Q20=makeQuery(id+"F6.imprint","IMPRINT",FACE,{"disambiguationData":[TD([[makeQuery(id+"F6.imprint","IMPRINT",EDGE,{"derivedFrom":sQuery(id+"F6.wireOp",EDGE,"E83")}),1.0]])]});
            var Q21;
            Q21=makeQuery(id+"F6.imprint","IMPRINT",FACE,{"disambiguationData":[TD([[makeQuery(id+"F6.imprint","IMPRINT",EDGE,{"derivedFrom":sQuery(id+"F6.wireOp",EDGE,"E79")}),1.0]])]});
            var Q22;
            Q22=makeQuery(id+"F6.imprint","IMPRINT",FACE,{"disambiguationData":[TD([[makeQuery(id+"F6.imprint","IMPRINT",EDGE,{"derivedFrom":sQuery(id+"F6.wireOp",EDGE,"124a1fa9-0a09-4ff6-a598-60100b825ab1")}),1.0]])]});
            var Q23;
            {var subQ6=sQuery(id+"F6.wireOp",EDGE,"E77");Q23=makeQuery(id+"F6.imprint","IMPRINT",FACE,{"disambiguationData":[TD([[makeQuery(id+"F6.imprint","IMPRINT",EDGE,{"derivedFrom":subQ6}),1.0]])]});}
            var Q24;
            {var subQ0=sQuery(id+"F6.wireOp",EDGE,"E70");Q24=makeQuery(id+"F6.imprint","IMPRINT",FACE,{"disambiguationData":[TD([[makeQuery(id+"F6.imprint","IMPRINT",EDGE,{"derivedFrom":subQ0}),1.0]])]});}
            var Q25;
            Q25=makeQuery(id+"F6.imprint","IMPRINT",FACE,{"disambiguationData":[TD([[makeQuery(id+"F6.imprint","IMPRINT",EDGE,{"derivedFrom":sQuery(id+"F6.wireOp",EDGE,"ad5f39e7-b0be-45d8-b2ef-0b74307add0c")}),1.0]])]});
            var Q26;
            {var subQ0=sQuery(id+"F6.wireOp",EDGE,"E72");Q26=makeQuery(id+"F6.imprint","IMPRINT",FACE,{"disambiguationData":[TD([[makeQuery(id+"F6.imprint","IMPRINT",EDGE,{"derivedFrom":subQ0}),1.0]])]});}
            var Q27;
            {var subQ5=sQuery(id+"F6.wireOp",EDGE,"E66");Q27=makeQuery(id+"F6.imprint","IMPRINT",FACE,{"disambiguationData":[TD([[makeQuery(id+"F6.imprint","IMPRINT",EDGE,{"derivedFrom":subQ5}),1.0]])]});}
            var Q28;
            {var subQ0=sQuery(id+"F6.wireOp",EDGE,"E67");var subQ1=makeQuery(id+"F1.opExtrude","CAP_EDGE",EDGE,{"disambiguationData":[OSD([sQuery(id+"F0.wireOp",EDGE,"E0.right")])],"isStart":true});var subQ2=makeQuery(id+"F6.imprint","INTERSECT",VERTEX,{"disambiguationData":[OD(0.0)],"derivedFrom":[subQ1,subQ0]});Q28=makeQuery(id+"F6.imprint","IMPRINT",FACE,{"disambiguationData":[TD([[makeQuery(id+"F6.imprint","IMPRINT",EDGE,{"disambiguationData":[TD([[subQ2,-1.0]])],"derivedFrom":subQ0}),1.0]])]});}
            var Q29;
            {var subQ9=sQuery(id+"F6.wireOp",EDGE,"E55");Q29=makeQuery(id+"F6.imprint","IMPRINT",FACE,{"disambiguationData":[TD([[makeQuery(id+"F6.imprint","IMPRINT",EDGE,{"derivedFrom":subQ9}),1.0]])]});}
            var Q30;
            {var subQ0=sQuery(id+"F6.wireOp",EDGE,"E65");Q30=makeQuery(id+"F6.imprint","IMPRINT",FACE,{"disambiguationData":[TD([[makeQuery(id+"F6.imprint","IMPRINT",EDGE,{"derivedFrom":subQ0}),1.0]])]});}
            var Q31;
            {var subQ4=sQuery(id+"F6.wireOp",EDGE,"E61");Q31=makeQuery(id+"F6.imprint","IMPRINT",FACE,{"disambiguationData":[TD([[makeQuery(id+"F6.imprint","IMPRINT",EDGE,{"derivedFrom":subQ4}),1.0]])]});}
            var Q32;
            {var subQ0=sQuery(id+"F6.wireOp",EDGE,"E49");Q32=makeQuery(id+"F6.imprint","IMPRINT",FACE,{"disambiguationData":[TD([[makeQuery(id+"F6.imprint","IMPRINT",EDGE,{"derivedFrom":subQ0}),1.0]])]});}
            var Q33;
            Q33=makeQuery(id+"F6.imprint","IMPRINT",FACE,{"disambiguationData":[TD([[makeQuery(id+"F6.imprint","IMPRINT",EDGE,{"derivedFrom":sQuery(id+"F6.wireOp",EDGE,"E46")}),1.0]])]});
            var Q34;
            Q34=makeQuery(id+"F6.imprint","IMPRINT",FACE,{"disambiguationData":[TD([[makeQuery(id+"F6.imprint","IMPRINT",EDGE,{"derivedFrom":sQuery(id+"F6.wireOp",EDGE,"E110")}),1.0]])]});
            var Q35;
            {var subQ0=sQuery(id+"F6.wireOp",EDGE,"E115");Q35=makeQuery(id+"F6.imprint","IMPRINT",FACE,{"disambiguationData":[TD([[makeQuery(id+"F6.imprint","IMPRINT",EDGE,{"derivedFrom":subQ0}),1.0]])]});}
            var Q36;
            {var subQ0=sQuery(id+"F6.wireOp",EDGE,"E106");Q36=makeQuery(id+"F6.imprint","IMPRINT",FACE,{"disambiguationData":[TD([[makeQuery(id+"F6.imprint","IMPRINT",EDGE,{"derivedFrom":subQ0}),1.0]])]});}
            var Q37;
            {var subQ0=sQuery(id+"F6.wireOp",EDGE,"E108");Q37=makeQuery(id+"F6.imprint","IMPRINT",FACE,{"disambiguationData":[TD([[makeQuery(id+"F6.imprint","IMPRINT",EDGE,{"derivedFrom":subQ0}),1.0]])]});}
            var Q38;
            {var subQ0=sQuery(id+"F6.wireOp",EDGE,"E168");var subQ1=makeQuery(id+"F6.imprint","IMPRINT",VERTEX,{"derivedFrom":subQ0});Q38=makeQuery(id+"F6.imprint","IMPRINT",FACE,{"disambiguationData":[TD([[makeQuery(id+"F6.imprint","IMPRINT",EDGE,{"disambiguationData":[TD([[subQ1,1.0]])],"derivedFrom":subQ0}),-1.0]])]});}
            var Q39;
            {var subQ0=sQuery(id+"F6.wireOp",EDGE,"E134");Q39=makeQuery(id+"F6.imprint","IMPRINT",FACE,{"disambiguationData":[TD([[makeQuery(id+"F6.imprint","IMPRINT",EDGE,{"derivedFrom":subQ0}),1.0]])]});}
            var Q40;
            {var subQ0=sQuery(id+"F6.wireOp",EDGE,"E43");Q40=makeQuery(id+"F6.imprint","IMPRINT",FACE,{"disambiguationData":[TD([[makeQuery(id+"F6.imprint","IMPRINT",EDGE,{"derivedFrom":subQ0}),1.0]])]});}
            var Q41;
            {var subQ6=sQuery(id+"F6.wireOp",EDGE,"E136");Q41=makeQuery(id+"F6.imprint","IMPRINT",FACE,{"disambiguationData":[TD([[makeQuery(id+"F6.imprint","IMPRINT",EDGE,{"derivedFrom":subQ6}),1.0]])]});}
            var Q42;
            Q42=makeQuery(id+"F6.imprint","IMPRINT",FACE,{"disambiguationData":[TD([[makeQuery(id+"F6.imprint","IMPRINT",EDGE,{"derivedFrom":sQuery(id+"F6.wireOp",EDGE,"E170")}),1.0]])]});
            var Q43;
            Q43=makeQuery(id+"F6.imprint","IMPRINT",FACE,{"disambiguationData":[TD([[makeQuery(id+"F6.imprint","IMPRINT",EDGE,{"derivedFrom":sQuery(id+"F6.wireOp",EDGE,"E171")}),1.0]])]});
            extrude(context, id + "F7", {"entities" : qUnion([Q0, Q1, Q2, Q3, Q4, Q5, Q6, Q7, Q8, Q9, Q10, Q11, Q12, Q13, Q14, Q15, Q16, Q17, Q18, Q19, Q20, Q21, Q22, Q23, Q24, Q25, Q26, Q27, Q28, Q29, Q30, Q31, Q32, Q33, Q34, Q35, Q36, Q37, Q38, Q39, Q40, Q41, Q42, Q43]), "depth" : 1 * mm, "offsetDistance" : 25 * mm});
        }
        {
            var Q0;
            Q0=makeQuery(id+"F7.opExtrude","CAP_FACE",FACE,{"disambiguationData":[OSD([sQuery(id+"F6.wireOp",EDGE,"E74"),sQuery(id+"F6.wireOp",EDGE,"E75"),sQuery(id+"F6.wireOp",EDGE,"E76"),sQuery(id+"F6.wireOp",EDGE,"E77"),sQuery(id+"F6.wireOp",EDGE,"E78")])],"isStart":true});
            var sketch = newSketch(context, id + "F8", { "sketchPlane" : qUnion([Q0])});
            skLineSegment(sketch, "E172.bottom", {"start": v(-23.2, 6.27) * mm, "end": v(21.88, 6.27) * mm});
            skLineSegment(sketch, "E172.top", {"start": v(-23.2, -5.95) * mm, "end": v(21.88, -5.95) * mm});
            skLineSegment(sketch, "E172.left", {"start": v(-23.2, 6.27) * mm, "end": v(-23.2, -5.95) * mm});
            skLineSegment(sketch, "E172.right", {"start": v(21.88, 6.27) * mm, "end": v(21.88, -5.95) * mm});
            skSolve(sketch);
        }
        {
            var Q0;
            Q0 = qSketchRegion(id + "F8", true);
            extrude(context, id + "F9", {"entities" : qUnion([Q0]), "operationType" : NewBodyOperationType.ADD, "depth" : .1 * mm, "offsetDistance" : 25 * mm});
        }
    });
